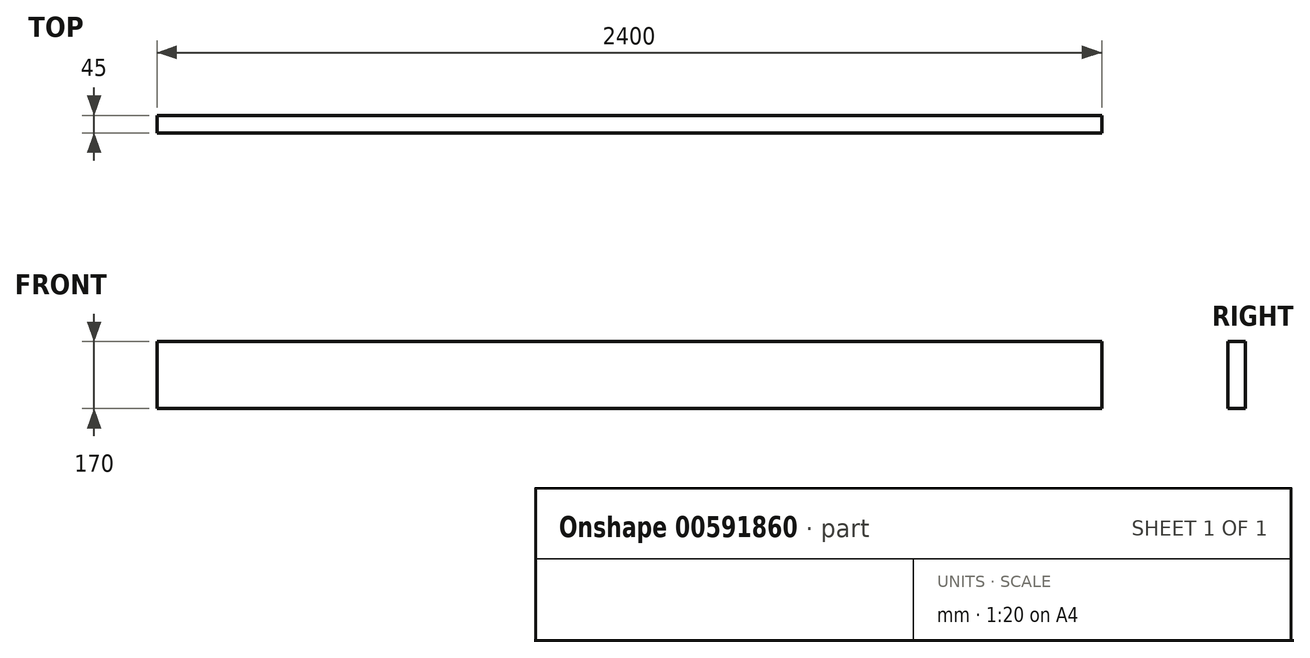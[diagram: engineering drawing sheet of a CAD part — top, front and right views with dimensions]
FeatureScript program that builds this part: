
annotation { "Feature Type Name" : "Feature", "Feature Type Description" : "" }
export const myFeature = defineFeature(function(context is Context, id is Id, definition is map)
    precondition{}
    {
        {
            var Q0;
            Q0=qCreatedBy(makeId("Front.planeOp"),FACE);
            var sketch = newSketch(context, id + "F0", { "sketchPlane" : qUnion([Q0])});
            skLineSegment(sketch, "E0.bottom", {"start": v(0, 0) * mm, "end": v(2400, 0) * mm});
            skLineSegment(sketch, "E0.top", {"start": v(0, 170) * mm, "end": v(2400, 170) * mm});
            skLineSegment(sketch, "E0.left", {"start": v(0, 0) * mm, "end": v(0, 170) * mm});
            skLineSegment(sketch, "E0.right", {"start": v(2400, 0) * mm, "end": v(2400, 170) * mm});
            skSolve(sketch);
        }
        {
            var Q0;
            Q0=makeQuery(id+"F0.imprint","IMPRINT",FACE,{"disambiguationData":[TD([[makeQuery(id+"F0.imprint","IMPRINT",EDGE,{"derivedFrom":sQuery(id+"F0.wireOp",EDGE,"E0.bottom")}),1.0]])]});
            extrude(context, id + "F1", {"entities" : qUnion([Q0]), "depth" : 45 * mm, "offsetDistance" : 25 * mm});
        }
    });
